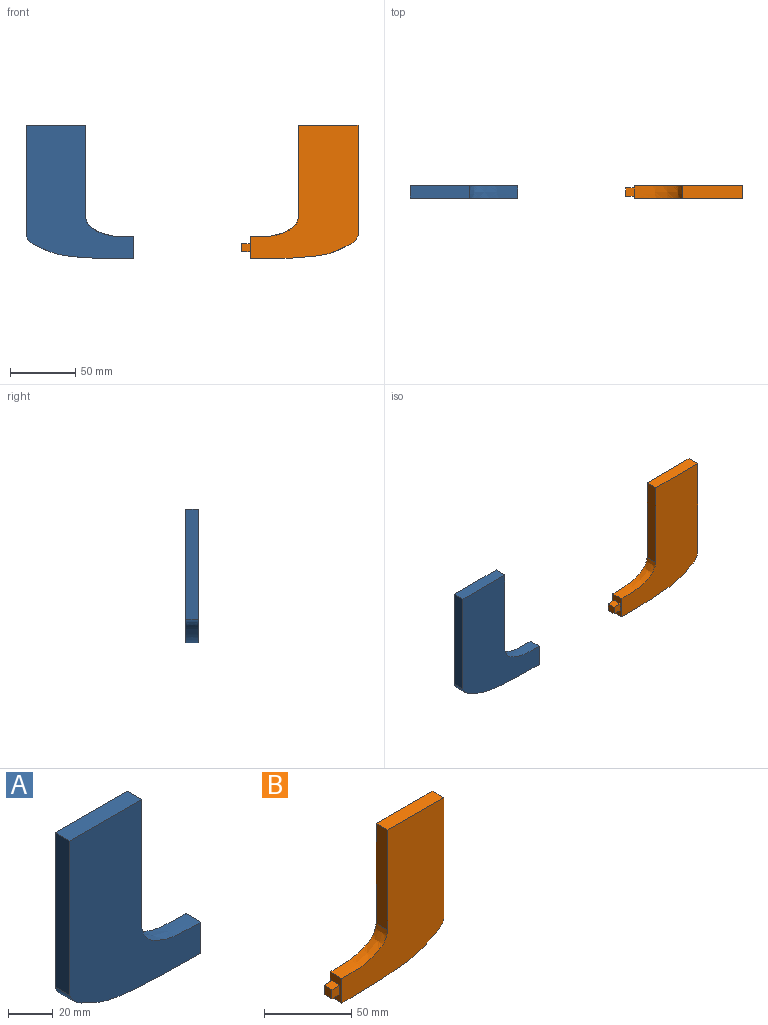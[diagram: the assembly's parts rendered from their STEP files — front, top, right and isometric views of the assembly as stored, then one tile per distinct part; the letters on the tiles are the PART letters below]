
ASSEMBLY  parts=2 mates=1
PART A: 13 faces, bbox 82.6x9.4x102.6 mm
  f0: plane 17.07x9.4mm, normal (1,0,0), area 120.1mm2, adj f1,f5,f6,f7,f8,f9,f10,f11
  f1: extruded ~37.17x15.46mm, area 413.2mm2, adj f0,f2,f6,f7
  f2: plane 69.99x9.4mm, normal (1,0,0), area 657.8mm2, adj f1,f3,f6,f7
  f3: plane 45.38x9.4mm, normal (0,0,1), area 426.5mm2, adj f2,f4,f6,f7
  f4: plane 84.18x9.4mm, normal (-1,0,0), area 791.1mm2, adj f3,f5,f6,f7
  f5: extruded ~82.55x18.3mm, area 825.8mm2, adj f0,f4,f6,f7
  f6: plane 102.64x82.55mm, normal (0,-1,0), area 5116mm2, adj f0,f1,f2,f3,f4,f5
  f7: plane 102.64x82.55mm, normal (0,1,0), area 5116mm2, adj f0,f1,f2,f3,f4,f5
  f8: plane 6.35x6.35mm, normal (0,0,1), area 40.3mm2, adj f0,f9,f11,f12
  f9: plane 6.35x6.35mm, normal (0,-1,0), area 40.3mm2, adj f0,f8,f10,f12
  f10: plane 6.35x6.35mm, normal (0,0,-1), area 40.3mm2, adj f0,f9,f11,f12
  f11: plane 6.35x6.35mm, normal (0,1,0), area 40.3mm2, adj f0,f8,f10,f12
  f12: plane 6.35x6.35mm, normal (1,0,0), area 40.3mm2, adj f8,f9,f10,f11
PART B: 14 faces, bbox 88.9x9.4x102.4 mm
  f0: extruded ~71.68x18.27mm, area 723.7mm2, adj f1,f6,f7,f8
  f1: plane 84.18x9.4mm, normal (1,0,0), area 791.1mm2, adj f0,f2,f7,f8
  f2: plane 45.38x9.4mm, normal (0,0,1), area 426.5mm2, adj f1,f3,f7,f8
  f3: plane 69.99x9.4mm, normal (-1,0,0), area 657.8mm2, adj f2,f4,f7,f8
  f4: extruded ~37.17x15.46mm, area 413.2mm2, adj f3,f5,f7,f8
  f5: plane 17.07x9.4mm, normal (-1,0,0), area 120.1mm2, adj f4,f6,f7,f8,f9,f10,f11,f12
  f6: plane 10.87x9.4mm, normal (0,0,-1), area 102.2mm2, adj f0,f5,f7,f8
  f7: plane 102.44x82.55mm, normal (0,-1,0), area 5115.8mm2, adj f0,f1,f2,f3,f4,f5,f6
  f8: plane 102.44x82.55mm, normal (0,1,0), area 5115.8mm2, adj f0,f1,f2,f3,f4,f5,f6
  f9: plane 6.35x6.35mm, normal (0,0,-1), area 40.3mm2, adj f5,f10,f12,f13
  f10: plane 6.35x6.35mm, normal (0,-1,0), area 40.3mm2, adj f5,f9,f11,f13
  f11: plane 6.35x6.35mm, normal (0,0,1), area 40.3mm2, adj f5,f10,f12,f13
  f12: plane 6.35x6.35mm, normal (0,1,0), area 40.3mm2, adj f5,f9,f11,f13
  f13: plane 6.35x6.35mm, normal (-1,0,0), area 40.3mm2, adj f9,f10,f11,f12
PLACE A t=(-62.62,-6.27,-70.43)mm
PLACE B t=(-9.03,-6.27,-70.43)mm fixed
MATE slider A.f12 <-> B.f13  axis (1,0,0) through (-104.28,-10.97,-113.12)mm
